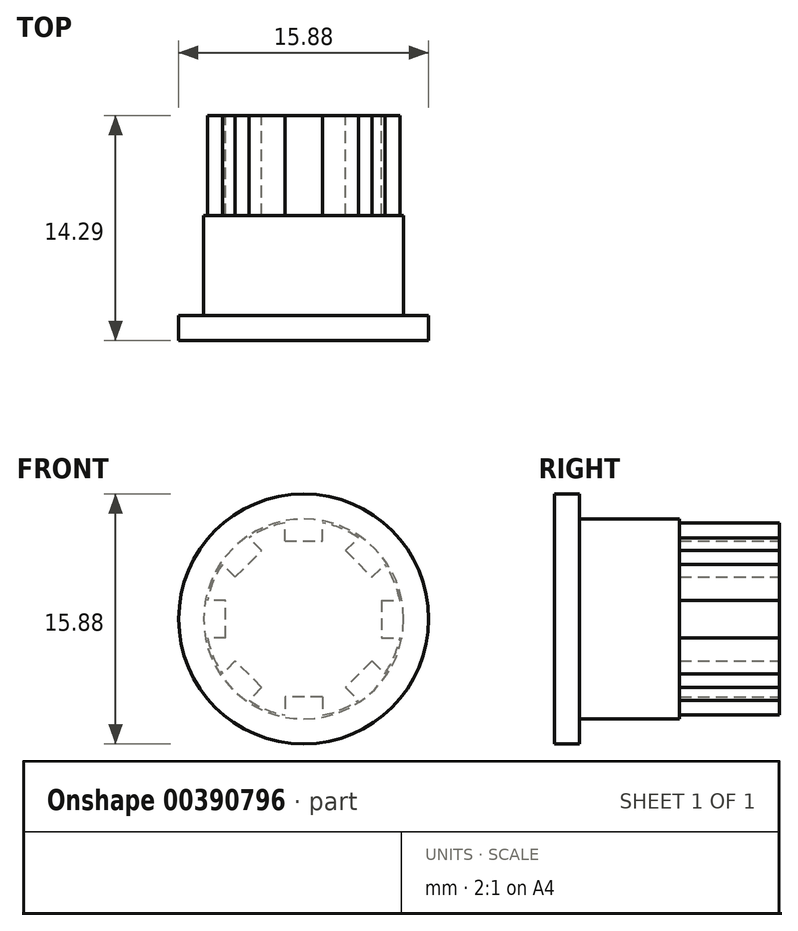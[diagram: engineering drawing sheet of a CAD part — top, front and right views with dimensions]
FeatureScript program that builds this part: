
annotation { "Feature Type Name" : "Feature", "Feature Type Description" : "" }
export const myFeature = defineFeature(function(context is Context, id is Id, definition is map)
    precondition{}
    {
        {
            var Q0;
            Q0=qCreatedBy(makeId("Front.planeOp"),FACE);
            var sketch = newSketch(context, id + "F0", { "sketchPlane" : qUnion([Q0]), "asVersion" : FeatureScriptVersionNumber.V593_MASTER_MODEL_DOC});
            skCircle(sketch, "E0", {"center": v(0, 0) * mm, "radius": 4.95 * mm, "construction": true});
            skArc(sketch, "E1", {"start": v(-1.2, 6.1) * mm, "mid": v(-2.38, 5.75) * mm, "end": v(-3.48, 5.16) * mm});
            skLineSegment(sketch, "E2", {"start": v(-1.2, 4.95) * mm, "end": v(1.2, 4.95) * mm});
            skPoint(sketch, "E3", {"position": v(0, 4.95) * mm});
            skLineSegment(sketch, "E4", {"start": v(-1.2, 4.95) * mm, "end": v(-1.2, 6.1) * mm});
            skLineSegment(sketch, "E5", {"start": v(1.2, 4.95) * mm, "end": v(1.2, 6.1) * mm});
            skLineSegment(sketch, "E6.1.0", {"start": v(-2.66, 4.34) * mm, "end": v(-3.48, 5.16) * mm});
            skLineSegment(sketch, "E6.1.1", {"start": v(-4.34, 2.66) * mm, "end": v(-2.66, 4.34) * mm});
            skLineSegment(sketch, "E6.1.2", {"start": v(-4.34, 2.66) * mm, "end": v(-5.16, 3.48) * mm});
            skLineSegment(sketch, "E6.2.0", {"start": v(-4.95, 1.2) * mm, "end": v(-6.1, 1.2) * mm});
            skLineSegment(sketch, "E6.2.1", {"start": v(-4.95, -1.2) * mm, "end": v(-4.95, 1.2) * mm});
            skLineSegment(sketch, "E6.2.2", {"start": v(-4.95, -1.2) * mm, "end": v(-6.1, -1.2) * mm});
            skLineSegment(sketch, "E6.3.0", {"start": v(-4.34, -2.66) * mm, "end": v(-5.16, -3.48) * mm});
            skLineSegment(sketch, "E6.3.1", {"start": v(-2.66, -4.34) * mm, "end": v(-4.34, -2.66) * mm});
            skLineSegment(sketch, "E6.3.2", {"start": v(-2.66, -4.34) * mm, "end": v(-3.48, -5.16) * mm});
            skLineSegment(sketch, "E6.4.0", {"start": v(-1.2, -4.95) * mm, "end": v(-1.2, -6.1) * mm});
            skLineSegment(sketch, "E6.4.1", {"start": v(1.2, -4.95) * mm, "end": v(-1.2, -4.95) * mm});
            skLineSegment(sketch, "E6.4.2", {"start": v(1.2, -4.95) * mm, "end": v(1.2, -6.1) * mm});
            skLineSegment(sketch, "E6.5.0", {"start": v(2.66, -4.34) * mm, "end": v(3.48, -5.16) * mm});
            skLineSegment(sketch, "E6.5.1", {"start": v(4.34, -2.66) * mm, "end": v(2.66, -4.34) * mm});
            skLineSegment(sketch, "E6.5.2", {"start": v(4.34, -2.66) * mm, "end": v(5.16, -3.48) * mm});
            skLineSegment(sketch, "E6.6.0", {"start": v(4.95, -1.2) * mm, "end": v(6.1, -1.2) * mm});
            skLineSegment(sketch, "E6.6.1", {"start": v(4.95, 1.2) * mm, "end": v(4.95, -1.2) * mm});
            skLineSegment(sketch, "E6.6.2", {"start": v(4.95, 1.2) * mm, "end": v(6.1, 1.2) * mm});
            skLineSegment(sketch, "E6.7.0", {"start": v(4.34, 2.66) * mm, "end": v(5.16, 3.48) * mm});
            skLineSegment(sketch, "E6.7.1", {"start": v(2.66, 4.34) * mm, "end": v(4.34, 2.66) * mm});
            skLineSegment(sketch, "E6.7.2", {"start": v(2.66, 4.34) * mm, "end": v(3.48, 5.16) * mm});
            skArc(sketch, "E7.trimOffspring", {"start": v(-5.16, 3.48) * mm, "mid": v(-5.75, 2.38) * mm, "end": v(-6.1, 1.2) * mm});
            skArc(sketch, "E8.trimOffspring", {"start": v(3.48, 5.16) * mm, "mid": v(2.38, 5.75) * mm, "end": v(1.2, 6.1) * mm});
            skArc(sketch, "E9.trimOffspring", {"start": v(6.1, 1.2) * mm, "mid": v(5.75, 2.38) * mm, "end": v(5.16, 3.48) * mm});
            skArc(sketch, "E10.trimOffspring", {"start": v(5.16, -3.48) * mm, "mid": v(5.75, -2.38) * mm, "end": v(6.1, -1.2) * mm});
            skArc(sketch, "E11.trimOffspring", {"start": v(1.2, -6.1) * mm, "mid": v(2.38, -5.75) * mm, "end": v(3.48, -5.16) * mm});
            skArc(sketch, "E12.trimOffspring", {"start": v(-3.48, -5.16) * mm, "mid": v(-2.38, -5.75) * mm, "end": v(-1.2, -6.1) * mm});
            skArc(sketch, "E13.trimOffspring", {"start": v(-6.1, -1.2) * mm, "mid": v(-5.75, -2.38) * mm, "end": v(-5.16, -3.48) * mm});
            skSolve(sketch);
        }
        {
            var Q0;
            Q0=makeQuery(id+"F0.imprint","IMPRINT",FACE,{"disambiguationData":[TD([[makeQuery(id+"F0.imprint","IMPRINT",EDGE,{"derivedFrom":sQuery(id+"F0.wireOp",EDGE,"E1")}),1.0]])]});
            extrude(context, id + "F1", {"entities" : qUnion([Q0]), "depth" : 6.35 * mm});
        }
        {
            var Q0;
            Q0=makeQuery(id+"F1.opExtrude","CAP_FACE",FACE,{"disambiguationData":[OSD([sQuery(id+"F0.wireOp",EDGE,"E1"),sQuery(id+"F0.wireOp",EDGE,"E2"),sQuery(id+"F0.wireOp",EDGE,"E4"),sQuery(id+"F0.wireOp",EDGE,"E5"),sQuery(id+"F0.wireOp",EDGE,"E6.1.0"),sQuery(id+"F0.wireOp",EDGE,"E6.1.1"),sQuery(id+"F0.wireOp",EDGE,"E6.1.2"),sQuery(id+"F0.wireOp",EDGE,"E6.2.0"),sQuery(id+"F0.wireOp",EDGE,"E6.2.1"),sQuery(id+"F0.wireOp",EDGE,"E6.2.2"),sQuery(id+"F0.wireOp",EDGE,"E6.3.0"),sQuery(id+"F0.wireOp",EDGE,"E6.3.1"),sQuery(id+"F0.wireOp",EDGE,"E6.3.2"),sQuery(id+"F0.wireOp",EDGE,"E6.4.0"),sQuery(id+"F0.wireOp",EDGE,"E6.4.1"),sQuery(id+"F0.wireOp",EDGE,"E6.4.2"),sQuery(id+"F0.wireOp",EDGE,"E6.5.0"),sQuery(id+"F0.wireOp",EDGE,"E6.5.1"),sQuery(id+"F0.wireOp",EDGE,"E6.5.2"),sQuery(id+"F0.wireOp",EDGE,"E6.6.0"),sQuery(id+"F0.wireOp",EDGE,"E6.6.1"),sQuery(id+"F0.wireOp",EDGE,"E6.6.2"),sQuery(id+"F0.wireOp",EDGE,"E6.7.0"),sQuery(id+"F0.wireOp",EDGE,"E6.7.1"),sQuery(id+"F0.wireOp",EDGE,"E6.7.2"),sQuery(id+"F0.wireOp",EDGE,"E7.trimOffspring"),sQuery(id+"F0.wireOp",EDGE,"E8.trimOffspring"),sQuery(id+"F0.wireOp",EDGE,"E9.trimOffspring"),sQuery(id+"F0.wireOp",EDGE,"E10.trimOffspring"),sQuery(id+"F0.wireOp",EDGE,"E11.trimOffspring"),sQuery(id+"F0.wireOp",EDGE,"E12.trimOffspring"),sQuery(id+"F0.wireOp",EDGE,"E13.trimOffspring")])],"isStart":false});
            var sketch = newSketch(context, id + "F2", { "sketchPlane" : qUnion([Q0]), "asVersion" : FeatureScriptVersionNumber.V593_MASTER_MODEL_DOC});
            skCircle(sketch, "E14", {"center": v(0, 0) * mm, "radius": 6.35 * mm});
            skSolve(sketch);
        }
        {
            var Q0;
            Q0=makeQuery(id+"F2.imprint","IMPRINT",FACE,{"disambiguationData":[TD([[makeQuery(id+"F2.imprint","IMPRINT",EDGE,{"derivedFrom":sQuery(id+"F2.wireOp",EDGE,"E14")}),1.0]])]});
            var Q1;
            Q1=makeQuery(id+"F2.imprint","IMPRINT",FACE,{"disambiguationData":[TD([[makeQuery(id+"F2.imprint","IMPRINT",EDGE,{"derivedFrom":makeQuery(id+"F1.opExtrude","CAP_EDGE",EDGE,{"disambiguationData":[OSD([sQuery(id+"F0.wireOp",EDGE,"E1")])],"isStart":false})}),1.0]])]});
            extrude(context, id + "F3", {"entities" : qUnion([Q0, Q1]), "operationType" : NewBodyOperationType.ADD, "depth" : 6.35 * mm});
        }
        {
            var Q0;
            Q0=makeQuery(id+"F3.opExtrude","CAP_FACE",FACE,{"disambiguationData":[OSD([sQuery(id+"F2.wireOp",EDGE,"E14")])],"isStart":false});
            var sketch = newSketch(context, id + "F4", { "sketchPlane" : qUnion([Q0]), "asVersion" : FeatureScriptVersionNumber.V593_MASTER_MODEL_DOC});
            skCircle(sketch, "E15", {"center": v(0, 0) * mm, "radius": 7.94 * mm});
            skSolve(sketch);
        }
        {
            var Q0;
            Q0=makeQuery(id+"F4.imprint","IMPRINT",FACE,{"disambiguationData":[TD([[makeQuery(id+"F4.imprint","IMPRINT",EDGE,{"derivedFrom":sQuery(id+"F4.wireOp",EDGE,"E15")}),1.0]])]});
            var Q1;
            Q1=makeQuery(id+"F4.imprint","IMPRINT",FACE,{"disambiguationData":[TD([[makeQuery(id+"F4.imprint","IMPRINT",EDGE,{"derivedFrom":makeQuery(id+"F3.opExtrude","CAP_EDGE",EDGE,{"disambiguationData":[OSD([sQuery(id+"F2.wireOp",EDGE,"E14")])],"isStart":false})}),1.0]])]});
            extrude(context, id + "F5", {"entities" : qUnion([Q0, Q1]), "operationType" : NewBodyOperationType.ADD, "depth" : 1.59 * mm});
        }
    });
